# Revit family: FU_Inspec_Carousel_2-2
name_source: partatom
category: Furniture
units: mm (PartAtom-declared; Revit-internal decimal feet)

## family parameters
Always vertical = Yes
Cut with Voids When Loaded = No
OmniClass Number = 23.40.20.00
OmniClass Title = General Furniture and Specialties
Room Calculation Point = No
Shared = No
Work Plane-Based = No

## types (3) — shared parameters
Assembly Code = E2020
Feet Material = Metal - Chrome - Polished
Frame Material = Metal - Chrome - Polished
Height = 810 mm
Keynote = 46.B
Manufacturer = Inspec
URL = https://inspecfurniture.com
Width = 620 mm  [stored 2.03412 ft]
zero-valued in all types: Default Elevation

## per-type parameters (varying)
| type | Back Inside Primary Material | Back Outside Material | Description | Model | Seat Material |
| Carousel 2.1 | Leather - Light Tan | Leather - Light Tan | Armchair on a 360° swivel chrome or black powder coat base. Upholstered seat and back. | Carousel 2.1 | Leather - Light Tan |
| Carousel 2.2 | Fabric - Orange | Fabric - Orange | Armchair on a 360° swivel chrome or black powder coat base on casters. Upholstered seat and back. | Carousel 2.2 | Fabric - Orange |
| Carousel 2.3 | Fabric - Grey Woven | Fabric - Grey Woven | Armchair on a 360° swivel chrome or black powder coat base on casters. Upholstered seat and back. | Carousel 2.2 | Fabric - Grey Woven |

note: [stored X ft] marks values corroborated as IEEE doubles in the binary element streams (Revit-internal decimal feet)

## geometry (parser evidence)
native form markers: Blend x12, Sweep x2
no freeform markers — native parametric forms only
